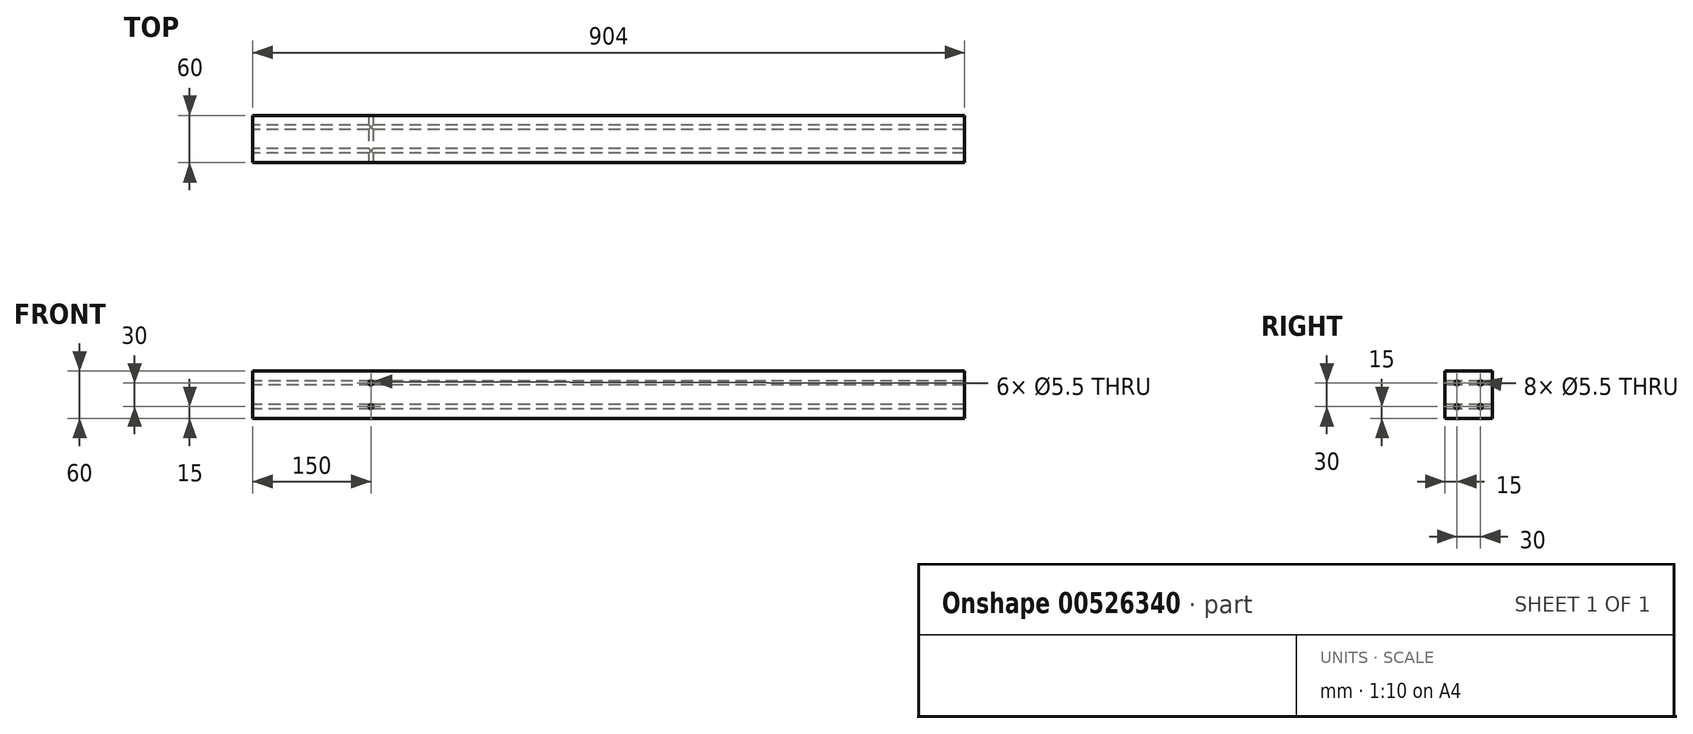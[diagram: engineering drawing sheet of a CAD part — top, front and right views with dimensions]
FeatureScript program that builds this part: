
annotation { "Feature Type Name" : "Feature", "Feature Type Description" : "" }
export const myFeature = defineFeature(function(context is Context, id is Id, definition is map)
    precondition{}
    {
        {
            var Q0;
            Q0=qCreatedBy(makeId("Right.planeOp"),FACE);
            var sketch = newSketch(context, id + "F0", { "sketchPlane" : qUnion([Q0])});
            skLineSegment(sketch, "E0.bottom", {"start": v(0, 0) * mm, "end": v(-60, 0) * mm});
            skLineSegment(sketch, "E0.top", {"start": v(0, 60) * mm, "end": v(-60, 60) * mm});
            skLineSegment(sketch, "E0.left", {"start": v(0, 0) * mm, "end": v(0, 60) * mm});
            skLineSegment(sketch, "E0.right", {"start": v(-60, 0) * mm, "end": v(-60, 60) * mm});
            skPoint(sketch, "E1", {"position": v(-45, 45) * mm});
            skPoint(sketch, "E2", {"position": v(-45, 15) * mm});
            skPoint(sketch, "E3", {"position": v(-15, 15) * mm});
            skPoint(sketch, "E4", {"position": v(-15, 45) * mm});
            skSolve(sketch);
        }
        {
            var Q0;
            Q0=makeQuery(id+"F0.imprint","IMPRINT",FACE,{"disambiguationData":[TD([[makeQuery(id+"F0.imprint","IMPRINT",EDGE,{"derivedFrom":sQuery(id+"F0.wireOp",EDGE,"E0.bottom")}),-1.0]])]});
            extrude(context, id + "F1", {"entities" : qUnion([Q0]), "depth" : 904 * mm, "offsetDistance" : 25 * mm});
        }
        {
            var Q0;
            Q0=sQuery(id+"F0.wireOp",VERTEX,"E1");
            var Q1;
            Q1=sQuery(id+"F0.wireOp",VERTEX,"E2");
            var Q2;
            Q2=sQuery(id+"F0.wireOp",VERTEX,"E3");
            var Q3;
            Q3=sQuery(id+"F0.wireOp",VERTEX,"E4");
            var Q4;
            Q4=makeQuery(id+"F1.opExtrude","SWEPT_BODY",BODY,{"disambiguationData":[OSD([sQuery(id+"F0.wireOp",EDGE,"E0.bottom"),sQuery(id+"F0.wireOp",EDGE,"E0.top"),sQuery(id+"F0.wireOp",EDGE,"E0.left"),sQuery(id+"F0.wireOp",EDGE,"E0.right")])]});
            hole(context, id + "F2", {"style" : HoleStyle.SIMPLE, "endStyle" : HoleEndStyle.THROUGH, "oppositeDirection" : true, "standardTappedOrClearance" : lookupTablePath({ "standard" : "ISO", "fit" : "Normal", "size" : "M5", "type" : "Clearance" }), "standardBlindInLast" : lookupTablePath({ "fit" : "Standard", "standard" : "ISO", "size" : "M5", "type" : "Clearance" }), "holeDiameter" : 5.5 * mm, "isTappedThrough" : true, "tappedDepth" : 12 * mm, "tapClearance" : 3, "locations" : qUnion([Q0, Q1, Q2, Q3]), "scope" : qUnion([Q4])});
        }
        {
            var Q0;
            Q0=makeQuery(id+"F1.opExtrude","SWEPT_FACE",FACE,{"disambiguationData":[OSD([sQuery(id+"F0.wireOp",EDGE,"E0.right")])]});
            var sketch = newSketch(context, id + "F3", { "sketchPlane" : qUnion([Q0])});
            skPoint(sketch, "E5", {"position": v(150, 45) * mm});
            skPoint(sketch, "E6", {"position": v(150, 15) * mm});
            skSolve(sketch);
        }
        {
            var Q0;
            Q0=sQuery(id+"F3.wireOp",VERTEX,"E5");
            var Q1;
            Q1=sQuery(id+"F3.wireOp",VERTEX,"E6");
            var Q2;
            Q2=makeQuery(id+"F1.opExtrude","SWEPT_BODY",BODY,{"disambiguationData":[OSD([sQuery(id+"F0.wireOp",EDGE,"E0.bottom"),sQuery(id+"F0.wireOp",EDGE,"E0.top"),sQuery(id+"F0.wireOp",EDGE,"E0.left"),sQuery(id+"F0.wireOp",EDGE,"E0.right")])]});
            hole(context, id + "F4", {"style" : HoleStyle.SIMPLE, "endStyle" : HoleEndStyle.THROUGH, "standardTappedOrClearance" : lookupTablePath({ "standard" : "ISO", "fit" : "Normal", "size" : "M5", "type" : "Clearance" }), "standardBlindInLast" : lookupTablePath({ "fit" : "Standard", "standard" : "ISO", "size" : "M5", "type" : "Clearance" }), "holeDiameter" : 5.5 * mm, "isTappedThrough" : true, "tappedDepth" : 12 * mm, "tapClearance" : 3, "locations" : qUnion([Q0, Q1]), "scope" : qUnion([Q2])});
        }
    });
